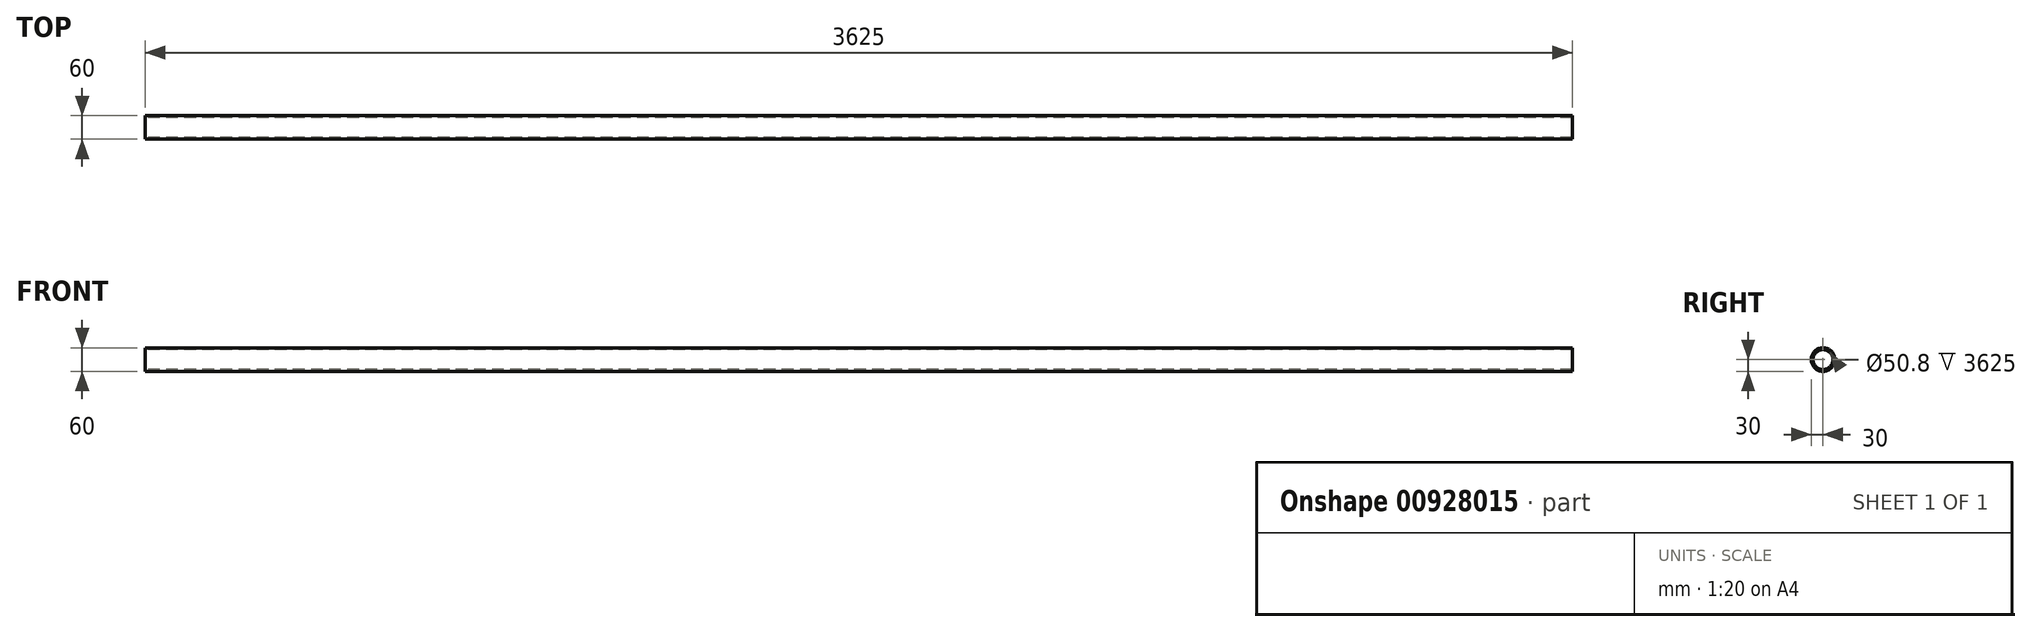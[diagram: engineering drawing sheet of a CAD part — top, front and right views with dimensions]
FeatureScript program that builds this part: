
annotation { "Feature Type Name" : "Feature", "Feature Type Description" : "" }
export const myFeature = defineFeature(function(context is Context, id is Id, definition is map)
    precondition{}
    {
        {
            var Q0;
            Q0=qCreatedBy(makeId("Right.planeOp"),FACE);
            var sketch = newSketch(context, id + "F0", { "sketchPlane" : qUnion([Q0])});
            skCircle(sketch, "E0", {"center": v(0, 0) * mm, "radius": 30 * mm});
            skCircle(sketch, "E1", {"center": v(0, 0) * mm, "radius": 25.4 * mm});
            skSolve(sketch);
        }
        {
            var Q0;
            Q0=qSketchRegion(id+"F0",true);
            extrude(context, id + "F1", {"entities" : qUnion([Q0]), "depth" : 3625 * mm, "offsetDistance" : 25 * mm});
        }
    });
